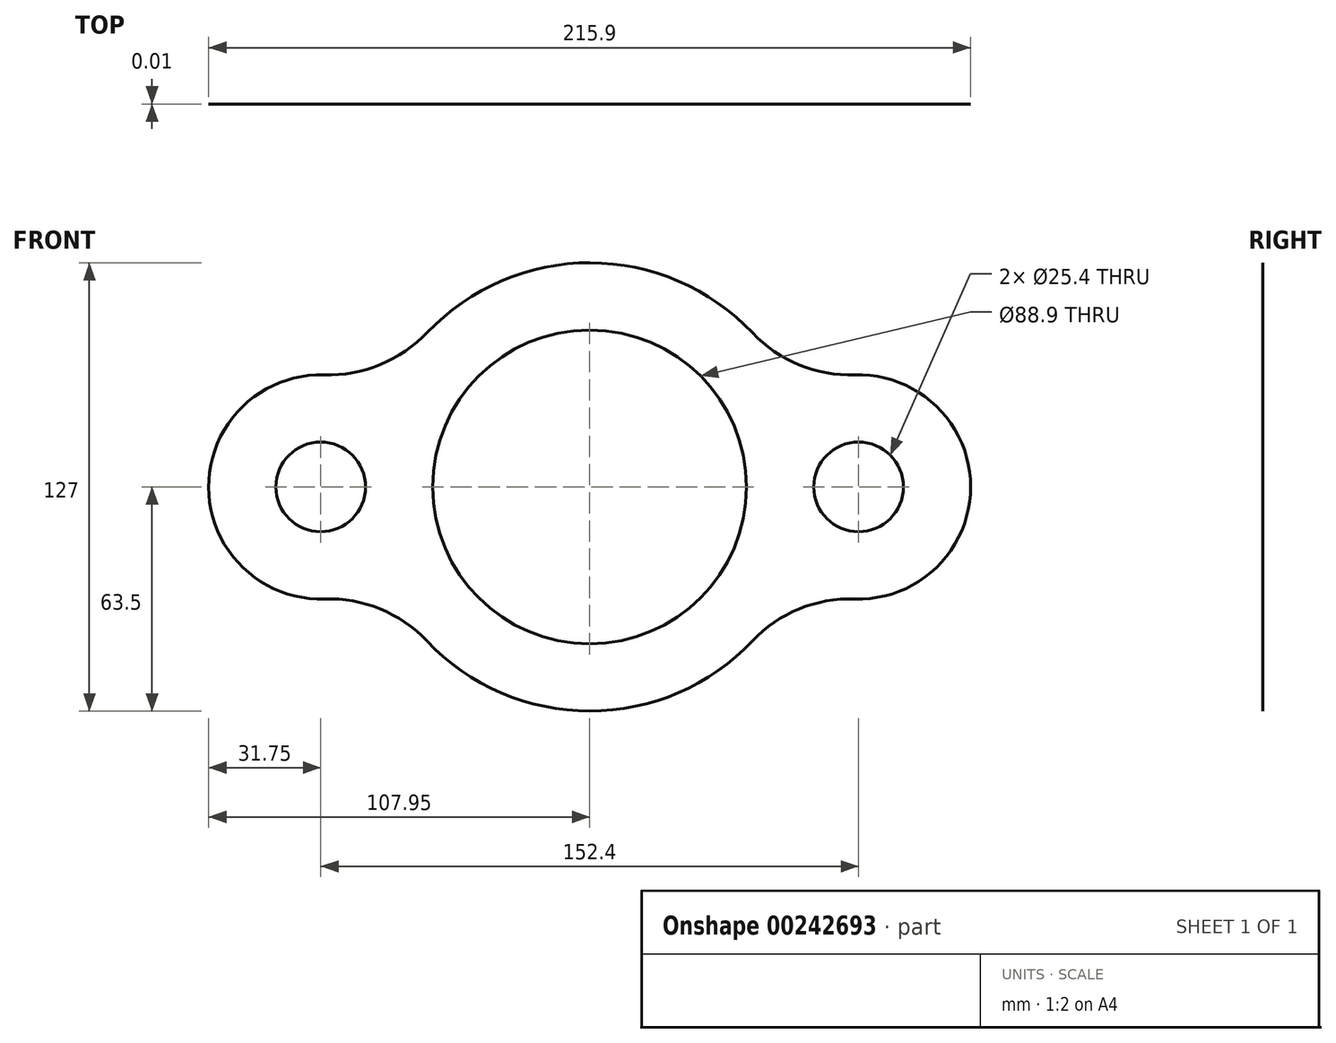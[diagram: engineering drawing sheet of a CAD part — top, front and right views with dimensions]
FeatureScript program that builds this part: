
annotation { "Feature Type Name" : "Feature", "Feature Type Description" : "" }
export const myFeature = defineFeature(function(context is Context, id is Id, definition is map)
    precondition{}
    {
        {
            var Q0;
            Q0=qCreatedBy(makeId("Front.planeOp"),FACE);
            var sketch = newSketch(context, id + "F0", { "sketchPlane" : qUnion([Q0])});
            skArc(sketch, "E0", {"start": v(-46.14, -43.63) * mm, "mid": v(0, -63.5) * mm, "end": v(46.14, -43.63) * mm});
            skCircle(sketch, "E1", {"center": v(0, 0) * mm, "radius": 44.45 * mm});
            skArc(sketch, "E2", {"start": v(-75.31, 31.74) * mm, "mid": v(-107.95, -0.1) * mm, "end": v(-75.12, -31.73) * mm});
            skArc(sketch, "E3", {"start": v(75.12, -31.73) * mm, "mid": v(107.95, 0) * mm, "end": v(75.12, 31.73) * mm});
            skCircle(sketch, "E4", {"center": v(76.2, 0) * mm, "radius": 12.7 * mm});
            skCircle(sketch, "E5", {"center": v(-76.2, 0) * mm, "radius": 12.7 * mm});
            skArc(sketch, "E6.trimOffspring", {"start": v(46.14, 43.63) * mm, "mid": v(0.13, 63.5) * mm, "end": v(-45.95, 43.82) * mm});
            skPoint(sketch, "E7.visualSharp", {"position": v(-57.94, 25.98) * mm});
            skArc(sketch, "E7.filletArc", {"start": v(-75.31, 31.74) * mm, "mid": v(-59.35, 34.66) * mm, "end": v(-45.95, 43.82) * mm});
            skPoint(sketch, "E8.visualSharp", {"position": v(57.94, 25.98) * mm});
            skArc(sketch, "E8.filletArc", {"start": v(46.14, 43.63) * mm, "mid": v(59.35, 34.56) * mm, "end": v(75.12, 31.73) * mm});
            skPoint(sketch, "E9.visualSharp", {"position": v(57.94, -25.98) * mm});
            skArc(sketch, "E9.filletArc", {"start": v(75.12, -31.73) * mm, "mid": v(59.35, -34.56) * mm, "end": v(46.14, -43.63) * mm});
            skPoint(sketch, "E10.visualSharp", {"position": v(-57.94, -25.98) * mm});
            skArc(sketch, "E10.filletArc", {"start": v(-46.14, -43.63) * mm, "mid": v(-59.35, -34.56) * mm, "end": v(-75.12, -31.73) * mm});
            skSolve(sketch);
        }
        {
            var Q0;
            Q0 = qSketchRegion(id + "F0", true);
            extrude(context, id + "F1", {"entities" : qUnion([Q0]), "depth" : 1 / 101.6 * mm});
        }
    });
